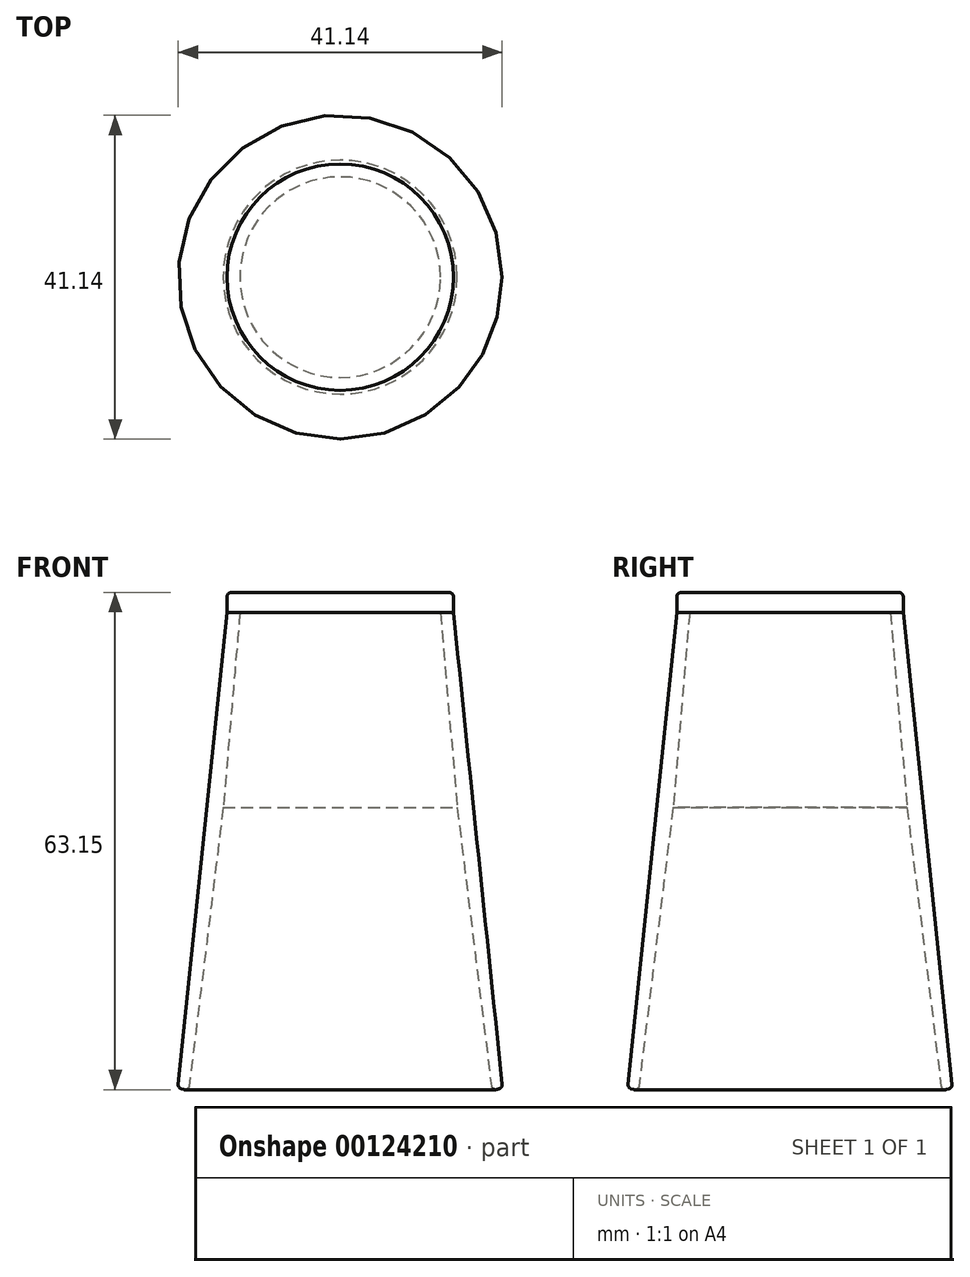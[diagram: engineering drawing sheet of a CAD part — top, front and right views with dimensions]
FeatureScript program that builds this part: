
annotation { "Feature Type Name" : "Feature", "Feature Type Description" : "" }
export const myFeature = defineFeature(function(context is Context, id is Id, definition is map)
    precondition{}
    {
        {
            var Q0;
            Q0=qCreatedBy(makeId("Top.planeOp"),FACE);
            var sketch = newSketch(context, id + "F0", { "sketchPlane" : qUnion([Q0])});
            skCircle(sketch, "E0", {"center": v(0, 17.62) * mm, "radius": 12.24 * mm});
            skSolve(sketch);
        }
        {
            var Q0;
            Q0=qCreatedBy(makeId("Right.planeOp"),FACE);
            var sketch = newSketch(context, id + "F1", { "sketchPlane" : qUnion([Q0])});
            skLineSegment(sketch, "E1", {"start": v(30.36, -0.38) * mm, "end": v(32.48, -25.15) * mm});
            skLineSegment(sketch, "E2", {"start": v(32.48, -25.15) * mm, "end": v(36.9, -61.14) * mm});
            skLineSegment(sketch, "E3", {"start": v(32, -0.38) * mm, "end": v(38.23, -60.75) * mm});
            skLineSegment(sketch, "E4", {"start": v(38.23, -60.75) * mm, "end": v(36.9, -61.14) * mm});
            skLineSegment(sketch, "E5", {"start": v(32, -0.38) * mm, "end": v(30.36, -0.38) * mm});
            skSolve(sketch);
        }
        {
            var Q0;
            Q0=makeQuery(id+"F1.imprint","IMPRINT",FACE,{"disambiguationData":[TD([[makeQuery(id+"F1.imprint","IMPRINT",EDGE,{"derivedFrom":sQuery(id+"F1.wireOp",EDGE,"E1")}),1.0]])]});
            var Q1;
            Q1=sQuery(id+"F0.wireOp",EDGE,"E0");
            revolve(context, id + "F2", {"entities" : qUnion([Q0]), "axis" : qUnion([Q1]), "revolveType" : RevolveType.FULL});
        }
        {
            var Q0;
            Q0=makeQuery(id+"F2.opRevolve","SWEPT_FACE",FACE,{"disambiguationData":[OSD([sQuery(id+"F1.wireOp",EDGE,"E5")])]});
            var sketch = newSketch(context, id + "F3", { "sketchPlane" : qUnion([Q0])});
            skCircle(sketch, "E6", {"center": v(0, 17.62) * mm, "radius": 14.38 * mm});
            skSolve(sketch);
        }
        {
            var Q0;
            Q0 = qSketchRegion(id + "F3", true);
            extrude(context, id + "F4", {"entities" : qUnion([Q0]), "operationType" : NewBodyOperationType.ADD, "depth" : 2.54 * mm});
        }
        {
            var Q0;
            Q0=makeQuery(id+"F2.opRevolve","SWEPT_EDGE",EDGE,{"disambiguationData":[OSD([sQuery(id+"F1.wireOp",EDGE,"E3"),sQuery(id+"F1.wireOp",EDGE,"E4")])]});
            var Q1;
            Q1=makeQuery(id+"F2.opRevolve","SWEPT_EDGE",EDGE,{"disambiguationData":[OSD([sQuery(id+"F1.wireOp",EDGE,"E2"),sQuery(id+"F1.wireOp",EDGE,"E4")])]});
            var Q2;
            Q2=makeQuery(id+"F4.opExtrude","CAP_EDGE",EDGE,{"disambiguationData":[OSD([sQuery(id+"F3.wireOp",EDGE,"E6")])],"isStart":false});
            fillet(context, id + "F5", {"entities" : qUnion([Q0, Q1, Q2]), "radius" : 0.5 * mm, "tangentPropagation" : true, "allowEdgeOverflow" : false});
        }
    });
